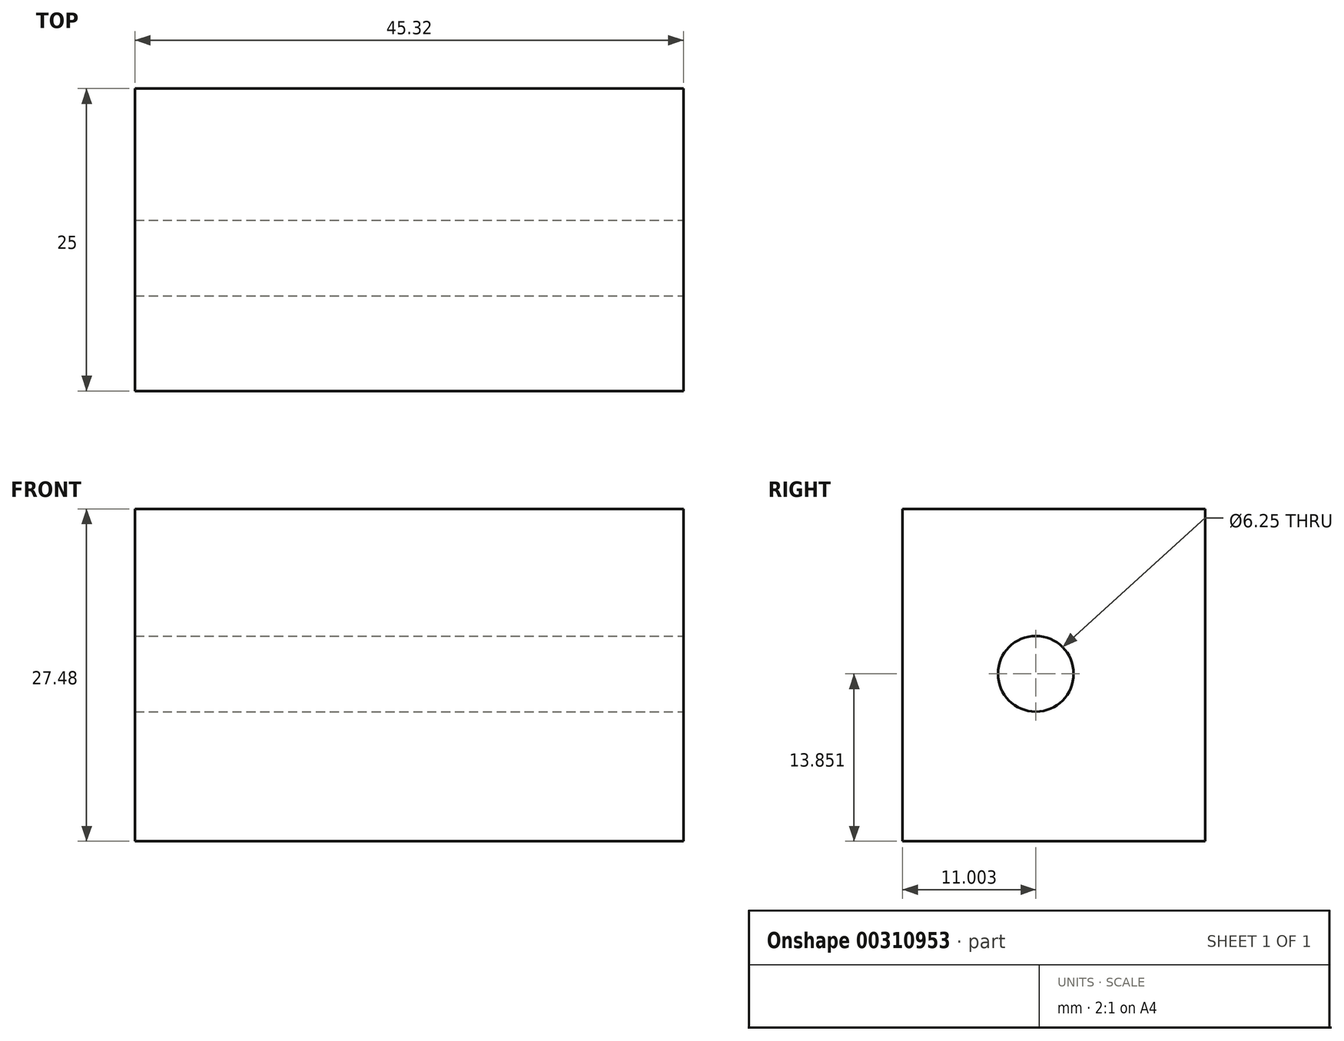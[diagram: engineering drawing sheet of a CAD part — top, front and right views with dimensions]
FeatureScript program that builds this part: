
annotation { "Feature Type Name" : "Feature", "Feature Type Description" : "" }
export const myFeature = defineFeature(function(context is Context, id is Id, definition is map)
    precondition{}
    {
        {
            var Q0;
            Q0=qCreatedBy(makeId("Front.planeOp"),FACE);
            var sketch = newSketch(context, id + "F0", { "sketchPlane" : qUnion([Q0])});
            skLineSegment(sketch, "E0.bottom", {"start": v(-35.83, 0) * mm, "end": v(9.49, 0) * mm});
            skLineSegment(sketch, "E0.top", {"start": v(-35.83, 27.48) * mm, "end": v(9.49, 27.48) * mm});
            skLineSegment(sketch, "E0.left", {"start": v(-35.83, 0) * mm, "end": v(-35.83, 27.48) * mm});
            skLineSegment(sketch, "E0.right", {"start": v(9.49, 0) * mm, "end": v(9.49, 27.48) * mm});
            skSolve(sketch);
        }
        {
            var Q0;
            Q0=makeQuery(id+"F0.imprint","IMPRINT",FACE,{"disambiguationData":[TD([[makeQuery(id+"F0.imprint","IMPRINT",EDGE,{"derivedFrom":sQuery(id+"F0.wireOp",EDGE,"E0.bottom")}),1.0]])]});
            extrude(context, id + "F1", {"entities" : qUnion([Q0]), "depth" : 25 * mm});
        }
        {
            var Q0;
            Q0=makeQuery(id+"F1.opExtrude","SWEPT_FACE",FACE,{"disambiguationData":[OSD([sQuery(id+"F0.wireOp",EDGE,"E0.right")])]});
            var sketch = newSketch(context, id + "F2", { "sketchPlane" : qUnion([Q0])});
            skCircle(sketch, "E1", {"center": v(-14, 13.85) * mm, "radius": 3.12 * mm});
            skSolve(sketch);
        }
        {
            var Q0;
            Q0=makeQuery(id+"F2.imprint","IMPRINT",FACE,{"disambiguationData":[TD([[makeQuery(id+"F2.imprint","IMPRINT",EDGE,{"derivedFrom":sQuery(id+"F2.wireOp",EDGE,"E1")}),1.0]])]});
            var Q1;
            Q1=sQuery(id+"F2.wireOp",EDGE,"E1");
            extrude(context, id + "F3", {"entities" : qUnion([Q0]), "operationType" : NewBodyOperationType.REMOVE, "surfaceEntities" : qUnion([Q1]), "endBound" : BoundingType.SYMMETRIC, "oppositeDirection" : true, "depth" : 100 * mm});
        }
    });
